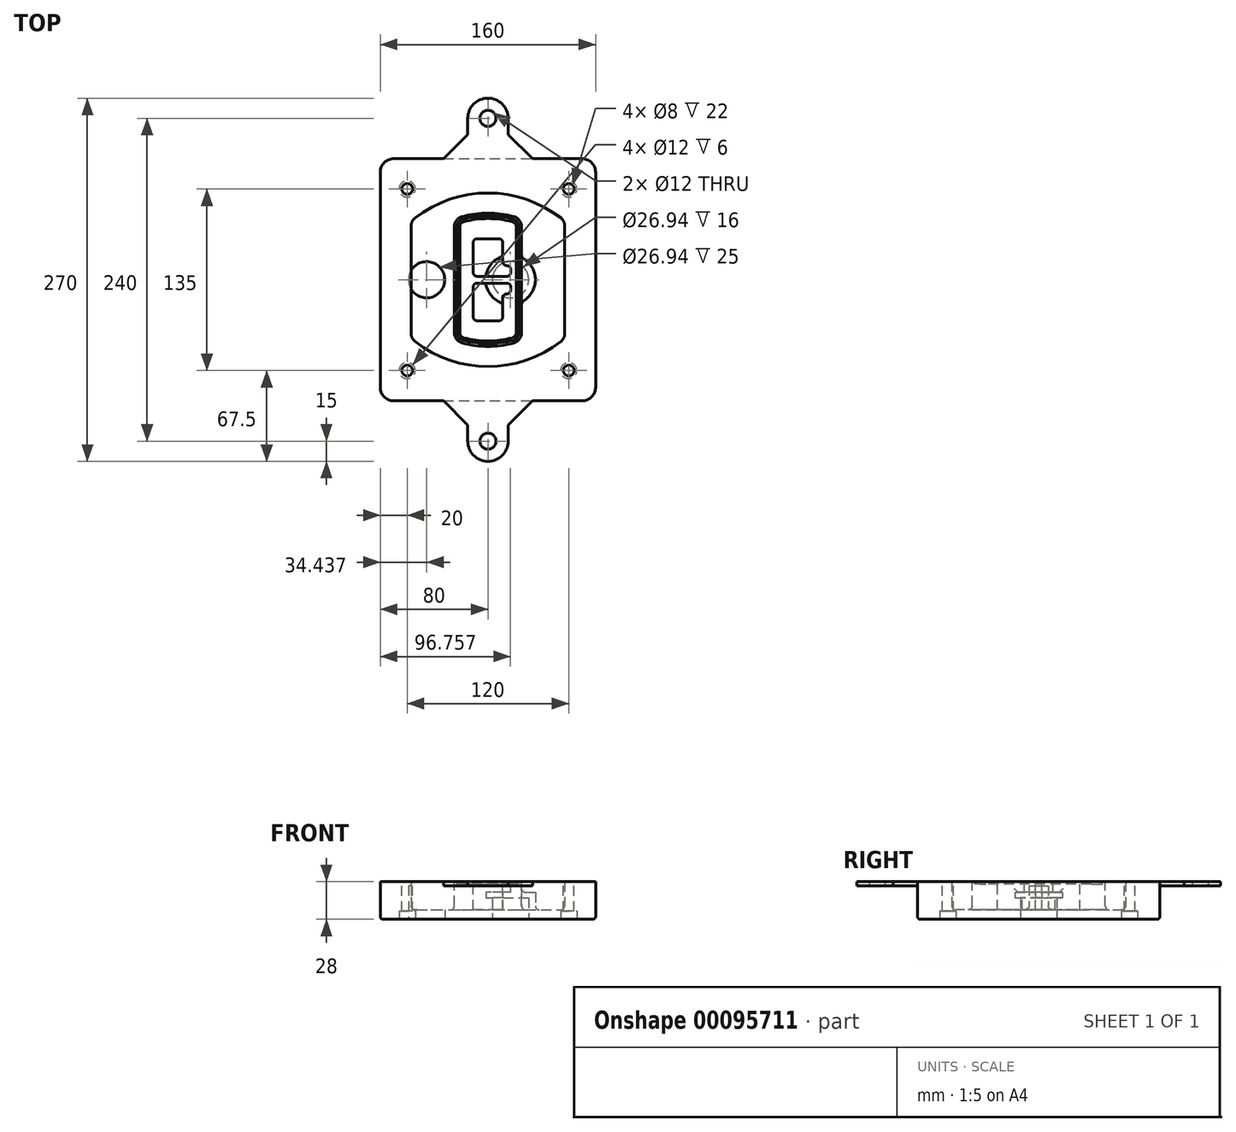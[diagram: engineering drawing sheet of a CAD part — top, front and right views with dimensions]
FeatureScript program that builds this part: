
annotation { "Feature Type Name" : "Feature", "Feature Type Description" : "" }
export const myFeature = defineFeature(function(context is Context, id is Id, definition is map)
    precondition{}
    {
        {
            var Q0;
            Q0=qCreatedBy(makeId("Top.planeOp"),FACE);
            var sketch = newSketch(context, id + "F0", { "sketchPlane" : qUnion([Q0])});
            skPoint(sketch, "E0.rect.middle", {"position": v(0, 0) * mm});
            skLineSegment(sketch, "E1.bottom", {"start": v(-70, -90) * mm, "end": v(70, -90) * mm});
            skLineSegment(sketch, "E1.top", {"start": v(-70, 90) * mm, "end": v(70, 90) * mm});
            skLineSegment(sketch, "E1.left", {"start": v(-80, -80) * mm, "end": v(-80, 80) * mm});
            skLineSegment(sketch, "E1.right", {"start": v(80, -80) * mm, "end": v(80, 80) * mm});
            skLineSegment(sketch, "E2", {"start": v(-80, 90) * mm, "end": v(80, -90) * mm, "construction": true});
            skLineSegment(sketch, "E3", {"start": v(80, 90) * mm, "end": v(-80, -90) * mm, "construction": true});
            skCircle(sketch, "E4", {"center": v(-60, 67.5) * mm, "radius": 4 * mm});
            skCircle(sketch, "E5", {"center": v(60, 67.5) * mm, "radius": 4 * mm});
            skCircle(sketch, "E6", {"center": v(60, -67.5) * mm, "radius": 4 * mm});
            skCircle(sketch, "E7", {"center": v(-60, -67.5) * mm, "radius": 4 * mm});
            skLineSegment(sketch, "E8", {"start": v(-60, 67.5) * mm, "end": v(60, 67.5) * mm, "construction": true});
            skLineSegment(sketch, "E9", {"start": v(60, 67.5) * mm, "end": v(60, -67.5) * mm, "construction": true});
            skLineSegment(sketch, "E10", {"start": v(60, -67.5) * mm, "end": v(-60, -67.5) * mm, "construction": true});
            skLineSegment(sketch, "E11", {"start": v(-60, -67.5) * mm, "end": v(-60, 67.5) * mm, "construction": true});
            skLineSegment(sketch, "E12", {"start": v(-60, 40.3) * mm, "end": v(-60, -40.3) * mm});
            skLineSegment(sketch, "E13", {"start": v(60, 40.3) * mm, "end": v(60, -40.3) * mm});
            skArc(sketch, "E14", {"start": v(56.15, 48.18) * mm, "mid": v(0, 67.5) * mm, "end": v(-56.15, 48.18) * mm});
            skArc(sketch, "E15", {"start": v(-56.15, -48.18) * mm, "mid": v(0, -67.5) * mm, "end": v(56.15, -48.18) * mm});
            skLineSegment(sketch, "E16", {"start": v(-60, 0) * mm, "end": v(60, 0) * mm, "construction": true});
            skPoint(sketch, "E17.visualSharp", {"position": v(-60, -45) * mm});
            skArc(sketch, "E17.filletArc", {"start": v(-60, -40.3) * mm, "mid": v(-58.99, -44.68) * mm, "end": v(-56.15, -48.18) * mm});
            skPoint(sketch, "E18.visualSharp", {"position": v(-60, 45) * mm});
            skArc(sketch, "E18.filletArc", {"start": v(-56.15, 48.18) * mm, "mid": v(-58.99, 44.68) * mm, "end": v(-60, 40.3) * mm});
            skPoint(sketch, "E19.visualSharp", {"position": v(60, 45) * mm});
            skArc(sketch, "E19.filletArc", {"start": v(60, 40.3) * mm, "mid": v(58.99, 44.68) * mm, "end": v(56.15, 48.18) * mm});
            skPoint(sketch, "E20.visualSharp", {"position": v(60, -45) * mm});
            skArc(sketch, "E20.filletArc", {"start": v(56.15, -48.18) * mm, "mid": v(58.99, -44.68) * mm, "end": v(60, -40.3) * mm});
            skPoint(sketch, "E21.visualSharp", {"position": v(-80, 90) * mm});
            skArc(sketch, "E21.filletArc", {"start": v(-70, 90) * mm, "mid": v(-77.07, 87.07) * mm, "end": v(-80, 80) * mm});
            skPoint(sketch, "E22.visualSharp", {"position": v(80, 90) * mm});
            skArc(sketch, "E22.filletArc", {"start": v(80, 80) * mm, "mid": v(77.07, 87.07) * mm, "end": v(70, 90) * mm});
            skPoint(sketch, "E23.visualSharp", {"position": v(80, -90) * mm});
            skArc(sketch, "E23.filletArc", {"start": v(70, -90) * mm, "mid": v(77.07, -87.07) * mm, "end": v(80, -80) * mm});
            skPoint(sketch, "E24.visualSharp", {"position": v(-80, -90) * mm});
            skArc(sketch, "E24.filletArc", {"start": v(-80, -80) * mm, "mid": v(-77.07, -87.07) * mm, "end": v(-70, -90) * mm});
            skArc(sketch, "E25.0", {"start": v(57, 40.3) * mm, "mid": v(56.3, 43.36) * mm, "end": v(54.3, 45.81) * mm});
            skLineSegment(sketch, "E25.1", {"start": v(57, 40.3) * mm, "end": v(57, -40.3) * mm});
            skArc(sketch, "E25.2", {"start": v(54.3, -45.81) * mm, "mid": v(56.3, -43.36) * mm, "end": v(57, -40.3) * mm});
            skArc(sketch, "E25.3", {"start": v(-54.3, -45.81) * mm, "mid": v(0, -64.5) * mm, "end": v(54.3, -45.81) * mm});
            skArc(sketch, "E25.4", {"start": v(-57, -40.3) * mm, "mid": v(-56.3, -43.36) * mm, "end": v(-54.3, -45.81) * mm});
            skArc(sketch, "E25.5", {"start": v(54.3, 45.81) * mm, "mid": v(0, 64.5) * mm, "end": v(-54.3, 45.81) * mm});
            skLineSegment(sketch, "E25.6", {"start": v(-57, 40.3) * mm, "end": v(-57, -40.3) * mm});
            skArc(sketch, "E25.7", {"start": v(-54.3, 45.81) * mm, "mid": v(-56.3, 43.36) * mm, "end": v(-57, 40.3) * mm});
            skArc(sketch, "E26.0", {"start": v(-58.62, 51.33) * mm, "mid": v(-62.58, 46.43) * mm, "end": v(-64, 40.3) * mm});
            skArc(sketch, "E26.1", {"start": v(58.62, 51.33) * mm, "mid": v(0, 71.5) * mm, "end": v(-58.62, 51.33) * mm});
            skArc(sketch, "E26.2", {"start": v(64, 40.3) * mm, "mid": v(62.58, 46.43) * mm, "end": v(58.62, 51.33) * mm});
            skLineSegment(sketch, "E26.3", {"start": v(64, 40.3) * mm, "end": v(64, -40.3) * mm});
            skArc(sketch, "E26.4", {"start": v(58.62, -51.33) * mm, "mid": v(62.58, -46.43) * mm, "end": v(64, -40.3) * mm});
            skLineSegment(sketch, "E26.5", {"start": v(-64, 40.3) * mm, "end": v(-64, -40.3) * mm});
            skArc(sketch, "E26.6", {"start": v(-58.62, -51.33) * mm, "mid": v(0, -71.5) * mm, "end": v(58.62, -51.33) * mm});
            skArc(sketch, "E26.7", {"start": v(-64, -40.3) * mm, "mid": v(-62.58, -46.43) * mm, "end": v(-58.62, -51.33) * mm});
            skSolve(sketch);
        }
        {
            var Q0;
            Q0=makeQuery(id+"F0.imprint","IMPRINT",FACE,{"disambiguationData":[TD([[makeQuery(id+"F0.imprint","IMPRINT",EDGE,{"derivedFrom":sQuery(id+"F0.wireOp",EDGE,"E1.bottom")}),1.0]])]});
            var Q1;
            Q1=makeQuery(id+"F0.imprint","IMPRINT",FACE,{"disambiguationData":[TD([[makeQuery(id+"F0.imprint","IMPRINT",EDGE,{"derivedFrom":sQuery(id+"F0.wireOp",EDGE,"E12")}),1.0]])]});
            var Q2;
            Q2=makeQuery(id+"F0.imprint","IMPRINT",FACE,{"disambiguationData":[TD([[makeQuery(id+"F0.imprint","IMPRINT",EDGE,{"derivedFrom":sQuery(id+"F0.wireOp",EDGE,"E25.0")}),1.0]])]});
            var Q3;
            Q3=makeQuery(id+"F0.imprint","IMPRINT",FACE,{"disambiguationData":[TD([[makeQuery(id+"F0.imprint","IMPRINT",EDGE,{"derivedFrom":sQuery(id+"F0.wireOp",EDGE,"E12")}),-1.0]])]});
            extrude(context, id + "F1", {"entities" : qUnion([Q0, Q1, Q2, Q3]), "oppositeDirection" : true, "depth" : 25 * mm});
        }
        {
            var Q0;
            Q0=makeQuery(id+"F0.imprint","IMPRINT",FACE,{"disambiguationData":[TD([[makeQuery(id+"F0.imprint","IMPRINT",EDGE,{"derivedFrom":sQuery(id+"F0.wireOp",EDGE,"E12")}),1.0]])]});
            extrude(context, id + "F2", {"entities" : qUnion([Q0]), "operationType" : NewBodyOperationType.ADD, "depth" : 3 * mm});
        }
        {
            var Q0;
            Q0=makeQuery(id+"F0.imprint","IMPRINT",FACE,{"disambiguationData":[TD([[makeQuery(id+"F0.imprint","IMPRINT",EDGE,{"derivedFrom":sQuery(id+"F0.wireOp",EDGE,"E25.0")}),1.0]])]});
            extrude(context, id + "F3", {"entities" : qUnion([Q0]), "operationType" : NewBodyOperationType.REMOVE, "oppositeDirection" : true, "depth" : 18 * mm, "offsetDistance" : 25 * mm});
        }
        {
            var Q0;
            Q0=makeQuery(id+"F2.opExtrude","CAP_FACE",FACE,{"disambiguationData":[OSD([sQuery(id+"F0.wireOp",EDGE,"E12"),sQuery(id+"F0.wireOp",EDGE,"E13"),sQuery(id+"F0.wireOp",EDGE,"E14"),sQuery(id+"F0.wireOp",EDGE,"E15"),sQuery(id+"F0.wireOp",EDGE,"E17.filletArc"),sQuery(id+"F0.wireOp",EDGE,"E18.filletArc"),sQuery(id+"F0.wireOp",EDGE,"E19.filletArc"),sQuery(id+"F0.wireOp",EDGE,"E20.filletArc"),sQuery(id+"F0.wireOp",EDGE,"E25.0"),sQuery(id+"F0.wireOp",EDGE,"E25.1"),sQuery(id+"F0.wireOp",EDGE,"E25.2"),sQuery(id+"F0.wireOp",EDGE,"E25.3"),sQuery(id+"F0.wireOp",EDGE,"E25.4"),sQuery(id+"F0.wireOp",EDGE,"E25.5"),sQuery(id+"F0.wireOp",EDGE,"E25.6"),sQuery(id+"F0.wireOp",EDGE,"E25.7")])],"isStart":false});
            var sketch = newSketch(context, id + "F4", { "sketchPlane" : qUnion([Q0])});
            skArc(sketch, "E27.0", {"start": v(-19.08, -46.97) * mm, "mid": v(0, -49.5) * mm, "end": v(19.08, -46.97) * mm});
            skArc(sketch, "E28.0", {"start": v(19.08, 46.97) * mm, "mid": v(0, 49.5) * mm, "end": v(-19.08, 46.97) * mm});
            skLineSegment(sketch, "E29", {"start": v(-25, 39.25) * mm, "end": v(-25, -39.25) * mm});
            skLineSegment(sketch, "E30", {"start": v(25, 39.25) * mm, "end": v(25, -39.25) * mm});
            skLineSegment(sketch, "E31", {"start": v(-25, 45.1) * mm, "end": v(25, 45.1) * mm, "construction": true});
            skLineSegment(sketch, "E32", {"start": v(-25, -45.1) * mm, "end": v(25, -45.1) * mm, "construction": true});
            skPoint(sketch, "E33.visualSharp", {"position": v(-25, 45.1) * mm});
            skArc(sketch, "E33.filletArc", {"start": v(-19.08, 46.97) * mm, "mid": v(-23.35, 44.11) * mm, "end": v(-25, 39.25) * mm});
            skPoint(sketch, "E34.visualSharp", {"position": v(25, 45.1) * mm});
            skArc(sketch, "E34.filletArc", {"start": v(25, 39.25) * mm, "mid": v(23.35, 44.11) * mm, "end": v(19.08, 46.97) * mm});
            skPoint(sketch, "E35.visualSharp", {"position": v(25, -45.1) * mm});
            skArc(sketch, "E35.filletArc", {"start": v(19.08, -46.97) * mm, "mid": v(23.35, -44.11) * mm, "end": v(25, -39.25) * mm});
            skPoint(sketch, "E36.visualSharp", {"position": v(-25, -45.1) * mm});
            skArc(sketch, "E36.filletArc", {"start": v(-25, -39.25) * mm, "mid": v(-23.35, -44.11) * mm, "end": v(-19.08, -46.97) * mm});
            skArc(sketch, "E37.0", {"start": v(54.3, 45.81) * mm, "mid": v(0, 64.5) * mm, "end": v(-54.3, 45.81) * mm});
            skArc(sketch, "E37.1", {"start": v(-54.3, 45.81) * mm, "mid": v(-56.3, 43.36) * mm, "end": v(-57, 40.3) * mm});
            skLineSegment(sketch, "E37.2", {"start": v(-57, 40.3) * mm, "end": v(-57, -40.3) * mm});
            skArc(sketch, "E37.3", {"start": v(-57, -40.3) * mm, "mid": v(-56.3, -43.36) * mm, "end": v(-54.3, -45.81) * mm});
            skArc(sketch, "E37.4", {"start": v(-54.3, -45.81) * mm, "mid": v(0, -64.5) * mm, "end": v(54.3, -45.81) * mm});
            skArc(sketch, "E37.5", {"start": v(54.3, -45.81) * mm, "mid": v(56.3, -43.36) * mm, "end": v(57, -40.3) * mm});
            skLineSegment(sketch, "E37.6", {"start": v(57, 40.3) * mm, "end": v(57, -40.3) * mm});
            skArc(sketch, "E37.7", {"start": v(57, 40.3) * mm, "mid": v(56.3, 43.36) * mm, "end": v(54.3, 45.81) * mm});
            skLineSegment(sketch, "E38.0", {"start": v(23, 39.25) * mm, "end": v(23, -39.25) * mm});
            skArc(sketch, "E38.1", {"start": v(18.56, -45.04) * mm, "mid": v(21.76, -42.9) * mm, "end": v(23, -39.25) * mm});
            skArc(sketch, "E38.2", {"start": v(-18.56, -45.04) * mm, "mid": v(0, -47.5) * mm, "end": v(18.56, -45.04) * mm});
            skArc(sketch, "E38.3", {"start": v(-23, -39.25) * mm, "mid": v(-21.76, -42.9) * mm, "end": v(-18.56, -45.04) * mm});
            skLineSegment(sketch, "E38.4", {"start": v(-23, 39.25) * mm, "end": v(-23, -39.25) * mm});
            skArc(sketch, "E38.5", {"start": v(23, 39.25) * mm, "mid": v(21.76, 42.9) * mm, "end": v(18.56, 45.04) * mm});
            skArc(sketch, "E38.6", {"start": v(-18.56, 45.04) * mm, "mid": v(-21.76, 42.9) * mm, "end": v(-23, 39.25) * mm});
            skArc(sketch, "E38.7", {"start": v(18.56, 45.04) * mm, "mid": v(0, 47.5) * mm, "end": v(-18.56, 45.04) * mm});
            skArc(sketch, "E39.0", {"start": v(21, 39.25) * mm, "mid": v(20.18, 41.68) * mm, "end": v(18.04, 43.1) * mm});
            skLineSegment(sketch, "E39.1", {"start": v(21, 39.25) * mm, "end": v(21, -39.25) * mm});
            skArc(sketch, "E39.2", {"start": v(18.04, -43.1) * mm, "mid": v(20.18, -41.68) * mm, "end": v(21, -39.25) * mm});
            skArc(sketch, "E39.3", {"start": v(-18.04, -43.1) * mm, "mid": v(0, -45.5) * mm, "end": v(18.04, -43.1) * mm});
            skArc(sketch, "E39.4", {"start": v(-21, -39.25) * mm, "mid": v(-20.18, -41.68) * mm, "end": v(-18.04, -43.1) * mm});
            skArc(sketch, "E39.5", {"start": v(18.04, 43.1) * mm, "mid": v(0, 45.5) * mm, "end": v(-18.04, 43.1) * mm});
            skLineSegment(sketch, "E39.6", {"start": v(-21, 39.25) * mm, "end": v(-21, -39.25) * mm});
            skArc(sketch, "E39.7", {"start": v(-18.04, 43.1) * mm, "mid": v(-20.18, 41.68) * mm, "end": v(-21, 39.25) * mm});
            skLineSegment(sketch, "E40", {"start": v(-25, 0) * mm, "end": v(25, 0) * mm, "construction": true});
            skLineSegment(sketch, "E41", {"start": v(-11, 5.5) * mm, "end": v(-11, 27.5) * mm});
            skLineSegment(sketch, "E42", {"start": v(-8, 30.5) * mm, "end": v(8, 30.5) * mm});
            skLineSegment(sketch, "E43", {"start": v(11, 27.5) * mm, "end": v(11, 13.5) * mm});
            skLineSegment(sketch, "E44", {"start": v(14, 10.5) * mm, "end": v(14, 10.5) * mm});
            skLineSegment(sketch, "E45", {"start": v(17, 7.5) * mm, "end": v(17, 5.5) * mm});
            skLineSegment(sketch, "E46", {"start": v(14, 2.5) * mm, "end": v(-8, 2.5) * mm});
            skPoint(sketch, "E47.visualSharp", {"position": v(-11, 30.5) * mm});
            skArc(sketch, "E47.filletArc", {"start": v(-8, 30.5) * mm, "mid": v(-10.12, 29.62) * mm, "end": v(-11, 27.5) * mm});
            skPoint(sketch, "E48.visualSharp", {"position": v(11, 30.5) * mm});
            skArc(sketch, "E48.filletArc", {"start": v(11, 27.5) * mm, "mid": v(10.12, 29.62) * mm, "end": v(8, 30.5) * mm});
            skPoint(sketch, "E49.visualSharp", {"position": v(11, 10.5) * mm});
            skArc(sketch, "E49.filletArc", {"start": v(11, 13.5) * mm, "mid": v(11.88, 11.38) * mm, "end": v(14, 10.5) * mm});
            skPoint(sketch, "E50.visualSharp", {"position": v(17, 10.5) * mm});
            skArc(sketch, "E50.filletArc", {"start": v(17, 7.5) * mm, "mid": v(16.12, 9.62) * mm, "end": v(14, 10.5) * mm});
            skPoint(sketch, "E51.visualSharp", {"position": v(17, 2.5) * mm});
            skArc(sketch, "E51.filletArc", {"start": v(14, 2.5) * mm, "mid": v(16.12, 3.38) * mm, "end": v(17, 5.5) * mm});
            skPoint(sketch, "E52.visualSharp", {"position": v(-11, 2.5) * mm});
            skArc(sketch, "E52.filletArc", {"start": v(-11, 5.5) * mm, "mid": v(-10.12, 3.38) * mm, "end": v(-8, 2.5) * mm});
            skLineSegment(sketch, "E53.0.MirrorCS", {"start": v(14, -2.5) * mm, "end": v(-8, -2.5) * mm});
            skArc(sketch, "E54.0.MirrorCS", {"start": v(-11, -5.5) * mm, "mid": v(-10.12, -3.38) * mm, "end": v(-8, -2.5) * mm});
            skLineSegment(sketch, "E55.0.MirrorCS", {"start": v(-11, -5.5) * mm, "end": v(-11, -27.5) * mm});
            skArc(sketch, "E56.0.MirrorCS", {"start": v(-8, -30.5) * mm, "mid": v(-10.12, -29.62) * mm, "end": v(-11, -27.5) * mm});
            skLineSegment(sketch, "E57.0.MirrorCS", {"start": v(-8, -30.5) * mm, "end": v(8, -30.5) * mm});
            skArc(sketch, "E58.0.MirrorCS", {"start": v(11, -27.5) * mm, "mid": v(10.12, -29.62) * mm, "end": v(8, -30.5) * mm});
            skLineSegment(sketch, "E59.0.MirrorCS", {"start": v(11, -27.5) * mm, "end": v(11, -13.5) * mm});
            skArc(sketch, "E60.0.MirrorCS", {"start": v(11, -13.5) * mm, "mid": v(11.88, -11.38) * mm, "end": v(14, -10.5) * mm});
            skArc(sketch, "E61.0.MirrorCS", {"start": v(17, -7.5) * mm, "mid": v(16.12, -9.62) * mm, "end": v(14, -10.5) * mm});
            skLineSegment(sketch, "E62.0.MirrorCS", {"start": v(17, -7.5) * mm, "end": v(17, -5.5) * mm});
            skArc(sketch, "E63.0.MirrorCS", {"start": v(14, -2.5) * mm, "mid": v(16.12, -3.38) * mm, "end": v(17, -5.5) * mm});
            skSolve(sketch);
        }
        {
            var Q0;
            Q0=makeQuery(id+"F4.imprint","IMPRINT",FACE,{"disambiguationData":[TD([[makeQuery(id+"F4.imprint","IMPRINT",EDGE,{"derivedFrom":sQuery(id+"F4.wireOp",EDGE,"E27.0")}),1.0]])]});
            var Q1;
            Q1=makeQuery(id+"F4.imprint","IMPRINT",FACE,{"disambiguationData":[TD([[makeQuery(id+"F4.imprint","IMPRINT",EDGE,{"derivedFrom":sQuery(id+"F4.wireOp",EDGE,"E38.0")}),-1.0]])]});
            var Q2;
            Q2=makeQuery(id+"F4.imprint","IMPRINT",FACE,{"disambiguationData":[TD([[makeQuery(id+"F4.imprint","IMPRINT",EDGE,{"derivedFrom":sQuery(id+"F4.wireOp",EDGE,"E39.0")}),1.0]])]});
            extrude(context, id + "F5", {"entities" : qUnion([Q0, Q1, Q2]), "operationType" : NewBodyOperationType.ADD, "endBound" : BoundingType.UP_TO_NEXT, "oppositeDirection" : true, "depth" : 25 * mm, "offsetDistance" : 25 * mm});
        }
        {
            var Q0;
            Q0=makeQuery(id+"F4.imprint","IMPRINT",FACE,{"disambiguationData":[TD([[makeQuery(id+"F4.imprint","IMPRINT",EDGE,{"derivedFrom":sQuery(id+"F4.wireOp",EDGE,"E38.0")}),-1.0]])]});
            extrude(context, id + "F6", {"entities" : qUnion([Q0]), "operationType" : NewBodyOperationType.REMOVE, "oppositeDirection" : true, "depth" : 2 * mm, "offsetDistance" : 25 * mm});
        }
        {
            var Q0;
            Q0=makeQuery(id+"F1.opExtrude","CAP_FACE",FACE,{"disambiguationData":[OSD([sQuery(id+"F0.wireOp",EDGE,"E1.bottom"),sQuery(id+"F0.wireOp",EDGE,"E1.top"),sQuery(id+"F0.wireOp",EDGE,"E1.left"),sQuery(id+"F0.wireOp",EDGE,"E1.right"),sQuery(id+"F0.wireOp",EDGE,"E4"),sQuery(id+"F0.wireOp",EDGE,"E5"),sQuery(id+"F0.wireOp",EDGE,"E6"),sQuery(id+"F0.wireOp",EDGE,"E7"),sQuery(id+"F0.wireOp",EDGE,"E21.filletArc"),sQuery(id+"F0.wireOp",EDGE,"E22.filletArc"),sQuery(id+"F0.wireOp",EDGE,"E23.filletArc"),sQuery(id+"F0.wireOp",EDGE,"E24.filletArc")])],"isStart":false});
            var sketch = newSketch(context, id + "F7", { "sketchPlane" : qUnion([Q0])});
            skCircle(sketch, "E64", {"center": v(16.76, 0) * mm, "radius": 13.47 * mm});
            skCircle(sketch, "E65", {"center": v(-45.56, 0) * mm, "radius": 13.47 * mm});
            skLineSegment(sketch, "E66", {"start": v(80, 0) * mm, "end": v(-80, 0) * mm});
            skCircle(sketch, "E67", {"center": v(16.76, 0) * mm, "radius": 18.47 * mm});
            skCircle(sketch, "E68", {"center": v(60, -67.5) * mm, "radius": 6 * mm});
            skCircle(sketch, "E69", {"center": v(-60, -67.5) * mm, "radius": 6 * mm});
            skCircle(sketch, "E70", {"center": v(-60, 67.5) * mm, "radius": 6 * mm});
            skCircle(sketch, "E71", {"center": v(60, 67.5) * mm, "radius": 6 * mm});
            skSolve(sketch);
        }
        {
            var Q0;
            {var subQ1=sQuery(id+"F7.wireOp",EDGE,"E66");var subQ4=sQuery(id+"F7.wireOp",EDGE,"E64");var subQ6=makeQuery(id+"F7.imprint","INTERSECT",VERTEX,{"disambiguationData":[OD(0.0)],"derivedFrom":[subQ4,subQ1]});Q0=makeQuery(id+"F7.imprint","IMPRINT",FACE,{"disambiguationData":[TD([[makeQuery(id+"F7.imprint","IMPRINT",EDGE,{"disambiguationData":[TD([[subQ6,-1.0]])],"derivedFrom":subQ4}),-1.0]])]});}
            var Q1;
            {var subQ0=sQuery(id+"F7.wireOp",EDGE,"E66");var subQ1=sQuery(id+"F7.wireOp",EDGE,"E64");var subQ3=makeQuery(id+"F7.imprint","INTERSECT",VERTEX,{"disambiguationData":[OD(0.0)],"derivedFrom":[subQ1,subQ0]});Q1=makeQuery(id+"F7.imprint","IMPRINT",FACE,{"disambiguationData":[TD([[makeQuery(id+"F7.imprint","IMPRINT",EDGE,{"disambiguationData":[TD([[subQ3,-1.0]])],"derivedFrom":subQ1}),1.0]])]});}
            var Q2;
            {var subQ0=sQuery(id+"F7.wireOp",EDGE,"E66");var subQ1=sQuery(id+"F7.wireOp",EDGE,"E64");var subQ3=makeQuery(id+"F7.imprint","INTERSECT",VERTEX,{"disambiguationData":[OD(0.0)],"derivedFrom":[subQ1,subQ0]});Q2=makeQuery(id+"F7.imprint","IMPRINT",FACE,{"disambiguationData":[TD([[makeQuery(id+"F7.imprint","IMPRINT",EDGE,{"disambiguationData":[TD([[subQ3,1.0]])],"derivedFrom":subQ1}),1.0]])]});}
            var Q3;
            {var subQ1=sQuery(id+"F7.wireOp",EDGE,"E66");var subQ4=sQuery(id+"F7.wireOp",EDGE,"E64");var subQ6=makeQuery(id+"F7.imprint","INTERSECT",VERTEX,{"disambiguationData":[OD(0.0)],"derivedFrom":[subQ4,subQ1]});Q3=makeQuery(id+"F7.imprint","IMPRINT",FACE,{"disambiguationData":[TD([[makeQuery(id+"F7.imprint","IMPRINT",EDGE,{"disambiguationData":[TD([[subQ6,1.0]])],"derivedFrom":subQ4}),-1.0]])]});}
            extrude(context, id + "F8", {"entities" : qUnion([Q0, Q1, Q2, Q3]), "operationType" : NewBodyOperationType.ADD, "oppositeDirection" : true, "depth" : 20 * mm});
        }
        {
            var Q0;
            {var subQ0=sQuery(id+"F7.wireOp",EDGE,"E66");var subQ1=sQuery(id+"F7.wireOp",EDGE,"E64");var subQ3=makeQuery(id+"F7.imprint","INTERSECT",VERTEX,{"disambiguationData":[OD(0.0)],"derivedFrom":[subQ1,subQ0]});Q0=makeQuery(id+"F7.imprint","IMPRINT",FACE,{"disambiguationData":[TD([[makeQuery(id+"F7.imprint","IMPRINT",EDGE,{"disambiguationData":[TD([[subQ3,-1.0]])],"derivedFrom":subQ1}),1.0]])]});}
            var Q1;
            {var subQ0=sQuery(id+"F7.wireOp",EDGE,"E66");var subQ1=sQuery(id+"F7.wireOp",EDGE,"E64");var subQ3=makeQuery(id+"F7.imprint","INTERSECT",VERTEX,{"disambiguationData":[OD(0.0)],"derivedFrom":[subQ1,subQ0]});Q1=makeQuery(id+"F7.imprint","IMPRINT",FACE,{"disambiguationData":[TD([[makeQuery(id+"F7.imprint","IMPRINT",EDGE,{"disambiguationData":[TD([[subQ3,1.0]])],"derivedFrom":subQ1}),1.0]])]});}
            extrude(context, id + "F9", {"entities" : qUnion([Q0, Q1]), "operationType" : NewBodyOperationType.REMOVE, "oppositeDirection" : true, "depth" : 16 * mm});
        }
        {
            var Q0;
            {var subQ0=sQuery(id+"F7.wireOp",EDGE,"E66");var subQ1=sQuery(id+"F7.wireOp",EDGE,"E65");var subQ3=makeQuery(id+"F7.imprint","INTERSECT",VERTEX,{"disambiguationData":[OD(0.0)],"derivedFrom":[subQ1,subQ0]});Q0=makeQuery(id+"F7.imprint","IMPRINT",FACE,{"disambiguationData":[TD([[makeQuery(id+"F7.imprint","IMPRINT",EDGE,{"disambiguationData":[TD([[subQ3,-1.0]])],"derivedFrom":subQ1}),1.0]])]});}
            var Q1;
            {var subQ0=sQuery(id+"F7.wireOp",EDGE,"E66");var subQ1=sQuery(id+"F7.wireOp",EDGE,"E65");var subQ3=makeQuery(id+"F7.imprint","INTERSECT",VERTEX,{"disambiguationData":[OD(0.0)],"derivedFrom":[subQ1,subQ0]});Q1=makeQuery(id+"F7.imprint","IMPRINT",FACE,{"disambiguationData":[TD([[makeQuery(id+"F7.imprint","IMPRINT",EDGE,{"disambiguationData":[TD([[subQ3,1.0]])],"derivedFrom":subQ1}),1.0]])]});}
            extrude(context, id + "F10", {"entities" : qUnion([Q0, Q1]), "operationType" : NewBodyOperationType.REMOVE, "oppositeDirection" : true, "depth" : 25 * mm});
        }
        {
            var Q0;
            Q0=makeQuery(id+"F7.imprint","IMPRINT",FACE,{"disambiguationData":[TD([[makeQuery(id+"F7.imprint","IMPRINT",EDGE,{"derivedFrom":sQuery(id+"F7.wireOp",EDGE,"E68")}),1.0]])]});
            var Q1;
            Q1=makeQuery(id+"F7.imprint","IMPRINT",FACE,{"disambiguationData":[TD([[makeQuery(id+"F7.imprint","IMPRINT",EDGE,{"derivedFrom":makeQuery(id+"F1.opExtrude","CAP_EDGE",EDGE,{"disambiguationData":[OSD([sQuery(id+"F0.wireOp",EDGE,"E5")])],"isStart":false})}),-1.0]])]});
            var Q2;
            Q2=makeQuery(id+"F7.imprint","IMPRINT",FACE,{"disambiguationData":[TD([[makeQuery(id+"F7.imprint","IMPRINT",EDGE,{"derivedFrom":sQuery(id+"F7.wireOp",EDGE,"E69")}),1.0]])]});
            var Q3;
            Q3=makeQuery(id+"F7.imprint","IMPRINT",FACE,{"disambiguationData":[TD([[makeQuery(id+"F7.imprint","IMPRINT",EDGE,{"derivedFrom":makeQuery(id+"F1.opExtrude","CAP_EDGE",EDGE,{"disambiguationData":[OSD([sQuery(id+"F0.wireOp",EDGE,"E4")])],"isStart":false})}),-1.0]])]});
            var Q4;
            Q4=makeQuery(id+"F7.imprint","IMPRINT",FACE,{"disambiguationData":[TD([[makeQuery(id+"F7.imprint","IMPRINT",EDGE,{"derivedFrom":sQuery(id+"F7.wireOp",EDGE,"E70")}),1.0]])]});
            var Q5;
            Q5=makeQuery(id+"F7.imprint","IMPRINT",FACE,{"disambiguationData":[TD([[makeQuery(id+"F7.imprint","IMPRINT",EDGE,{"derivedFrom":makeQuery(id+"F1.opExtrude","CAP_EDGE",EDGE,{"disambiguationData":[OSD([sQuery(id+"F0.wireOp",EDGE,"E7")])],"isStart":false})}),-1.0]])]});
            var Q6;
            Q6=makeQuery(id+"F7.imprint","IMPRINT",FACE,{"disambiguationData":[TD([[makeQuery(id+"F7.imprint","IMPRINT",EDGE,{"derivedFrom":sQuery(id+"F7.wireOp",EDGE,"E71")}),1.0]])]});
            var Q7;
            Q7=makeQuery(id+"F7.imprint","IMPRINT",FACE,{"disambiguationData":[TD([[makeQuery(id+"F7.imprint","IMPRINT",EDGE,{"derivedFrom":makeQuery(id+"F1.opExtrude","CAP_EDGE",EDGE,{"disambiguationData":[OSD([sQuery(id+"F0.wireOp",EDGE,"E6")])],"isStart":false})}),-1.0]])]});
            extrude(context, id + "F11", {"entities" : qUnion([Q0, Q1, Q2, Q3, Q4, Q5, Q6, Q7]), "operationType" : NewBodyOperationType.REMOVE, "oppositeDirection" : true, "depth" : 6 * mm});
        }
        {
            var Q0;
            Q0=makeQuery(id+"F9.boolean.opBoolean","COPY",FACE,{"derivedFrom":makeQuery(id+"F9.opExtrude","CAP_FACE",FACE,{"disambiguationData":[OSD([sQuery(id+"F7.wireOp",EDGE,"E64")])],"isStart":false})});
            var sketch = newSketch(context, id + "F12", { "sketchPlane" : qUnion([Q0])});
            skArc(sketch, "E72.0", {"start": v(11, 17.55) * mm, "mid": v(2.57, 11.82) * mm, "end": v(-1.54, 2.5) * mm});
            skArc(sketch, "E72.1", {"start": v(-1.54, -2.5) * mm, "mid": v(2.57, -11.82) * mm, "end": v(11, -17.55) * mm});
            skLineSegment(sketch, "E73", {"start": v(-1.54, -2.5) * mm, "end": v(14, -2.5) * mm});
            skLineSegment(sketch, "E74.0", {"start": v(14, 2.5) * mm, "end": v(-1.54, 2.5) * mm});
            skArc(sketch, "E74.1", {"start": v(14, 2.5) * mm, "mid": v(16.12, 3.38) * mm, "end": v(17, 5.5) * mm});
            skLineSegment(sketch, "E74.2", {"start": v(17, 7.5) * mm, "end": v(17, 5.5) * mm});
            skArc(sketch, "E74.3", {"start": v(17, 7.5) * mm, "mid": v(16.12, 9.62) * mm, "end": v(14, 10.5) * mm});
            skArc(sketch, "E74.4", {"start": v(11, 13.5) * mm, "mid": v(11.88, 11.38) * mm, "end": v(14, 10.5) * mm});
            skLineSegment(sketch, "E74.5", {"start": v(11, 17.55) * mm, "end": v(11, 13.5) * mm});
            skLineSegment(sketch, "E74.7", {"start": v(14, -2.5) * mm, "end": v(-1.54, -2.5) * mm});
            skArc(sketch, "E74.8", {"start": v(14, -2.5) * mm, "mid": v(16.12, -3.38) * mm, "end": v(17, -5.5) * mm});
            skLineSegment(sketch, "E74.9", {"start": v(17, -7.5) * mm, "end": v(17, -5.5) * mm});
            skArc(sketch, "E74.10", {"start": v(17, -7.5) * mm, "mid": v(16.12, -9.62) * mm, "end": v(14, -10.5) * mm});
            skArc(sketch, "E74.11", {"start": v(11, -13.5) * mm, "mid": v(11.88, -11.38) * mm, "end": v(14, -10.5) * mm});
            skLineSegment(sketch, "E74.12", {"start": v(11, -17.55) * mm, "end": v(11, -13.5) * mm});
            skPoint(sketch, "E75.orphan", {"position": v(11, -27.5) * mm});
            skPoint(sketch, "E76.orphan", {"position": v(-8, -2.5) * mm});
            skPoint(sketch, "E77.orphan", {"position": v(-8, 2.5) * mm});
            skPoint(sketch, "E78.orphan", {"position": v(11, 27.5) * mm});
            skSolve(sketch);
        }
        {
            var Q0;
            {var subQ7=sQuery(id+"F12.wireOp",EDGE,"E72.0");var subQ14=sQuery(id+"F12.wireOp",EDGE,"E72.1");var subQ16=sQuery(id+"F12.wireOp",EDGE,"E74.1");var subQ18=sQuery(id+"F12.wireOp",EDGE,"E74.8");Q0=qUnion([makeQuery(id+"F12.imprint","IMPRINT",FACE,{"disambiguationData":[TD([[makeQuery(id+"F12.imprint","IMPRINT",EDGE,{"derivedFrom":subQ7}),1.0]])]}),makeQuery(id+"F12.imprint","IMPRINT",FACE,{"disambiguationData":[TD([[makeQuery(id+"F12.imprint","IMPRINT",EDGE,{"derivedFrom":subQ14}),1.0]])]}),makeQuery(id+"F12.imprint","IMPRINT",FACE,{"disambiguationData":[TD([[makeQuery(id+"F12.imprint","IMPRINT",EDGE,{"derivedFrom":subQ16}),1.0]])]}),makeQuery(id+"F12.imprint","IMPRINT",FACE,{"disambiguationData":[TD([[makeQuery(id+"F12.imprint","IMPRINT",EDGE,{"derivedFrom":subQ18}),-1.0]])]})]);}
            var Q1;
            Q1=makeQuery(id+"F5.boolean.opBoolean","SPLIT",FACE,{"disambiguationData":[TD([makeQuery(id+"F5.opExtrude","SWEPT_FACE",FACE,{"disambiguationData":[OSD([sQuery(id+"F4.wireOp",EDGE,"E41")])]})])],"derivedFrom":makeQuery(id+"F3.boolean.opBoolean","COPY",FACE,{"derivedFrom":makeQuery(id+"F3.opExtrude","CAP_FACE",FACE,{"disambiguationData":[OSD([sQuery(id+"F0.wireOp",EDGE,"E25.0"),sQuery(id+"F0.wireOp",EDGE,"E25.1"),sQuery(id+"F0.wireOp",EDGE,"E25.2"),sQuery(id+"F0.wireOp",EDGE,"E25.3"),sQuery(id+"F0.wireOp",EDGE,"E25.4"),sQuery(id+"F0.wireOp",EDGE,"E25.5"),sQuery(id+"F0.wireOp",EDGE,"E25.6"),sQuery(id+"F0.wireOp",EDGE,"E25.7")])],"isStart":false})})});
            extrude(context, id + "F13", {"entities" : qUnion([Q0]), "operationType" : NewBodyOperationType.REMOVE, "endBound" : BoundingType.UP_TO_SURFACE, "endBoundEntityFace" : qUnion([Q1]), "depth" : 25 * mm});
        }
        {
            var Q0;
            Q0=makeQuery(id+"F3.boolean.opBoolean","COPY",EDGE,{"derivedFrom":makeQuery(id+"F3.opExtrude","CAP_EDGE",EDGE,{"disambiguationData":[OSD([sQuery(id+"F0.wireOp",EDGE,"E25.6")])],"isStart":false})});
            var Q1;
            Q1=makeQuery(id+"F8.boolean.opBoolean","INTERSECT",EDGE,{"derivedFrom":[makeQuery(id+"F5.opExtrude","SWEPT_FACE",FACE,{"disambiguationData":[OSD([sQuery(id+"F4.wireOp",EDGE,"E30")])]}),makeQuery(id+"F8.opExtrude","CAP_FACE",FACE,{"disambiguationData":[OSD([sQuery(id+"F7.wireOp",EDGE,"E67")])],"isStart":false})]});
            var Q2;
            Q2=makeQuery(id+"F8.boolean.opBoolean","INTERSECT",EDGE,{"disambiguationData":[OD(1.0)],"derivedFrom":[makeQuery(id+"F5.opExtrude","SWEPT_FACE",FACE,{"disambiguationData":[OSD([sQuery(id+"F4.wireOp",EDGE,"E30")])]}),makeQuery(id+"F8.opExtrude","SWEPT_FACE",FACE,{"disambiguationData":[OSD([sQuery(id+"F7.wireOp",EDGE,"E67")])]})]});
            var Q3;
            {var subQ0=sQuery(id+"F4.wireOp",EDGE,"E30");Q3=makeQuery(id+"F8.boolean.opBoolean","SPLIT",EDGE,{"disambiguationData":[TD([makeQuery(id+"F5.opExtrude","SWEPT_FACE",FACE,{"disambiguationData":[OSD([sQuery(id+"F4.wireOp",EDGE,"E35.filletArc")])]})])],"derivedFrom":makeQuery(id+"F5.opExtrude","CAP_EDGE",EDGE,{"disambiguationData":[OSD([subQ0])],"isStart":false})});}
            var Q4;
            {var subQ0=sQuery(id+"F0.wireOp",EDGE,"E25.7");var subQ1=sQuery(id+"F0.wireOp",EDGE,"E25.1");var subQ2=sQuery(id+"F0.wireOp",EDGE,"E25.6");var subQ3=sQuery(id+"F0.wireOp",EDGE,"E25.5");var subQ4=sQuery(id+"F0.wireOp",EDGE,"E25.4");var subQ5=sQuery(id+"F0.wireOp",EDGE,"E25.0");var subQ6=sQuery(id+"F0.wireOp",EDGE,"E25.2");var subQ7=sQuery(id+"F0.wireOp",EDGE,"E25.3");Q4=makeQuery(id+"F8.boolean.opBoolean","INTERSECT",EDGE,{"derivedFrom":[makeQuery(id+"F5.boolean.opBoolean","SPLIT",FACE,{"disambiguationData":[TD([makeQuery(id+"F2.opExtrude","SWEPT_FACE",FACE,{"disambiguationData":[OSD([subQ5])]})])],"derivedFrom":makeQuery(id+"F3.boolean.opBoolean","COPY",FACE,{"derivedFrom":makeQuery(id+"F3.opExtrude","CAP_FACE",FACE,{"disambiguationData":[OSD([subQ5,subQ1,subQ6,subQ7,subQ4,subQ3,subQ2,subQ0])],"isStart":false})})}),makeQuery(id+"F8.opExtrude","SWEPT_FACE",FACE,{"disambiguationData":[OSD([sQuery(id+"F7.wireOp",EDGE,"E67")])]})]});}
            var Q5;
            Q5=makeQuery(id+"F8.boolean.opBoolean","INTERSECT",EDGE,{"disambiguationData":[OD(0.0)],"derivedFrom":[makeQuery(id+"F5.opExtrude","SWEPT_FACE",FACE,{"disambiguationData":[OSD([sQuery(id+"F4.wireOp",EDGE,"E30")])]}),makeQuery(id+"F8.opExtrude","SWEPT_FACE",FACE,{"disambiguationData":[OSD([sQuery(id+"F7.wireOp",EDGE,"E67")])]})]});
            fillet(context, id + "F14", {"entities" : qUnion([Q0, Q1, Q2, Q3, Q4, Q5]), "radius" : 3 * mm, "tangentPropagation" : true, "allowEdgeOverflow" : false});
        }
        {
            var Q0;
            Q0=makeQuery(id+"F1.opExtrude","CAP_EDGE",EDGE,{"disambiguationData":[OSD([sQuery(id+"F0.wireOp",EDGE,"E1.bottom")])],"isStart":false});
            fillet(context, id + "F15", {"entities" : qUnion([Q0]), "radius" : 2 * mm, "tangentPropagation" : true, "allowEdgeOverflow" : false});
        }
        {
            var Q0;
            {var subQ0=sQuery(id+"F0.wireOp",EDGE,"E22.filletArc");var subQ1=sQuery(id+"F0.wireOp",EDGE,"E7");var subQ2=sQuery(id+"F0.wireOp",EDGE,"E6");var subQ3=sQuery(id+"F0.wireOp",EDGE,"E5");var subQ4=sQuery(id+"F0.wireOp",EDGE,"E4");var subQ5=sQuery(id+"F0.wireOp",EDGE,"E1.bottom");var subQ6=sQuery(id+"F0.wireOp",EDGE,"E21.filletArc");var subQ7=sQuery(id+"F0.wireOp",EDGE,"E1.top");var subQ8=sQuery(id+"F0.wireOp",EDGE,"E1.left");var subQ9=sQuery(id+"F0.wireOp",EDGE,"E1.right");var subQ10=sQuery(id+"F0.wireOp",EDGE,"E23.filletArc");var subQ11=sQuery(id+"F0.wireOp",EDGE,"E24.filletArc");Q0=makeQuery(id+"F2.boolean.opBoolean","SPLIT",FACE,{"disambiguationData":[TD([makeQuery(id+"F1.opExtrude","SWEPT_FACE",FACE,{"disambiguationData":[OSD([subQ5])]})])],"derivedFrom":makeQuery(id+"F1.opExtrude","CAP_FACE",FACE,{"disambiguationData":[OSD([subQ5,subQ7,subQ8,subQ9,subQ4,subQ3,subQ2,subQ1,subQ6,subQ0,subQ10,subQ11])],"isStart":true})});}
            var sketch = newSketch(context, id + "F16", { "sketchPlane" : qUnion([Q0])});
            skLineSegment(sketch, "E79", {"start": v(-33, 90) * mm, "end": v(-15, 108) * mm});
            skLineSegment(sketch, "E80", {"start": v(33, 90) * mm, "end": v(15, 108) * mm});
            skLineSegment(sketch, "E81", {"start": v(15, 108) * mm, "end": v(15, 120) * mm});
            skLineSegment(sketch, "E82", {"start": v(-15, 108) * mm, "end": v(-15, 120) * mm});
            skCircle(sketch, "E83", {"center": v(0, 120) * mm, "radius": 6 * mm});
            skArc(sketch, "E84", {"start": v(15, 120) * mm, "mid": v(0, 135) * mm, "end": v(-15, 120) * mm});
            skLineSegment(sketch, "E85", {"start": v(0, 90) * mm, "end": v(0, 120) * mm, "construction": true});
            skLineSegment(sketch, "E86", {"start": v(-80, 0) * mm, "end": v(80, 0) * mm, "construction": true});
            skLineSegment(sketch, "E87.MirrorCS", {"start": v(0, -90) * mm, "end": v(0, -120) * mm, "construction": true});
            skLineSegment(sketch, "E88.MirrorCS", {"start": v(-33, -90) * mm, "end": v(-15, -108) * mm});
            skLineSegment(sketch, "E89.MirrorCS", {"start": v(33, -90) * mm, "end": v(15, -108) * mm});
            skLineSegment(sketch, "E90.MirrorCS", {"start": v(15, -108) * mm, "end": v(15, -120) * mm});
            skLineSegment(sketch, "E91.MirrorCS", {"start": v(-15, -108) * mm, "end": v(-15, -120) * mm});
            skArc(sketch, "E92.MirrorCS", {"start": v(15, -120) * mm, "mid": v(0, -135) * mm, "end": v(-15, -120) * mm});
            skCircle(sketch, "E93.MirrorC", {"center": v(0, -120) * mm, "radius": 6 * mm});
            skLineSegment(sketch, "E94", {"start": v(-70, 90) * mm, "end": v(70, 90) * mm, "construction": true});
            skSolve(sketch);
        }
        {
            var Q0;
            Q0=makeQuery(id+"F0.imprint","IMPRINT",FACE,{"disambiguationData":[TD([[makeQuery(id+"F0.imprint","IMPRINT",EDGE,{"derivedFrom":sQuery(id+"F0.wireOp",EDGE,"E1.bottom")}),1.0]])]});
            var Q1;
            Q1=makeQuery(id+"F0.imprint","IMPRINT",FACE,{"disambiguationData":[TD([[makeQuery(id+"F0.imprint","IMPRINT",EDGE,{"derivedFrom":sQuery(id+"F0.wireOp",EDGE,"E12")}),-1.0]])]});
            var Q2;
            Q2=makeQuery(id+"F2.opExtrude","CAP_FACE",FACE,{"disambiguationData":[OSD([sQuery(id+"F0.wireOp",EDGE,"E12"),sQuery(id+"F0.wireOp",EDGE,"E13"),sQuery(id+"F0.wireOp",EDGE,"E14"),sQuery(id+"F0.wireOp",EDGE,"E15"),sQuery(id+"F0.wireOp",EDGE,"E17.filletArc"),sQuery(id+"F0.wireOp",EDGE,"E18.filletArc"),sQuery(id+"F0.wireOp",EDGE,"E19.filletArc"),sQuery(id+"F0.wireOp",EDGE,"E20.filletArc"),sQuery(id+"F0.wireOp",EDGE,"E25.0"),sQuery(id+"F0.wireOp",EDGE,"E25.1"),sQuery(id+"F0.wireOp",EDGE,"E25.2"),sQuery(id+"F0.wireOp",EDGE,"E25.3"),sQuery(id+"F0.wireOp",EDGE,"E25.4"),sQuery(id+"F0.wireOp",EDGE,"E25.5"),sQuery(id+"F0.wireOp",EDGE,"E25.6"),sQuery(id+"F0.wireOp",EDGE,"E25.7")])],"isStart":false});
            extrude(context, id + "F17", {"entities" : qUnion([Q0, Q1]), "endBound" : BoundingType.UP_TO_SURFACE, "endBoundEntityFace" : qUnion([Q2]), "depth" : 25 * mm});
        }
        {
            var Q0;
            {var subQ1=sQuery(id+"F16.wireOp",EDGE,"E79");Q0=makeQuery(id+"F16.imprint","IMPRINT",FACE,{"disambiguationData":[TD([[makeQuery(id+"F16.imprint","IMPRINT",EDGE,{"derivedFrom":subQ1}),-1.0]])]});}
            var Q1;
            {var subQ1=sQuery(id+"F16.wireOp",EDGE,"E88.MirrorCS");Q1=makeQuery(id+"F16.imprint","IMPRINT",FACE,{"disambiguationData":[TD([[makeQuery(id+"F16.imprint","IMPRINT",EDGE,{"derivedFrom":subQ1}),1.0]])]});}
            var Q2;
            Q2=makeQuery(id+"F17.opExtrude","CAP_FACE",FACE,{"disambiguationData":[OSD([sQuery(id+"F0.wireOp",EDGE,"E1.bottom"),sQuery(id+"F0.wireOp",EDGE,"E1.top"),sQuery(id+"F0.wireOp",EDGE,"E1.left"),sQuery(id+"F0.wireOp",EDGE,"E1.right"),sQuery(id+"F0.wireOp",EDGE,"E4"),sQuery(id+"F0.wireOp",EDGE,"E5"),sQuery(id+"F0.wireOp",EDGE,"E6"),sQuery(id+"F0.wireOp",EDGE,"E7"),sQuery(id+"F0.wireOp",EDGE,"E12"),sQuery(id+"F0.wireOp",EDGE,"E13"),sQuery(id+"F0.wireOp",EDGE,"E14"),sQuery(id+"F0.wireOp",EDGE,"E15"),sQuery(id+"F0.wireOp",EDGE,"E17.filletArc"),sQuery(id+"F0.wireOp",EDGE,"E18.filletArc"),sQuery(id+"F0.wireOp",EDGE,"E19.filletArc"),sQuery(id+"F0.wireOp",EDGE,"E20.filletArc"),sQuery(id+"F0.wireOp",EDGE,"E21.filletArc"),sQuery(id+"F0.wireOp",EDGE,"E22.filletArc"),sQuery(id+"F0.wireOp",EDGE,"E23.filletArc"),sQuery(id+"F0.wireOp",EDGE,"E24.filletArc")])],"isStart":false});
            extrude(context, id + "F18", {"entities" : qUnion([Q0, Q1]), "operationType" : NewBodyOperationType.ADD, "endBound" : BoundingType.UP_TO_SURFACE, "endBoundEntityFace" : qUnion([Q2]), "offsetDistance" : 25 * mm, "depth" : 25 * mm});
        }
    });
